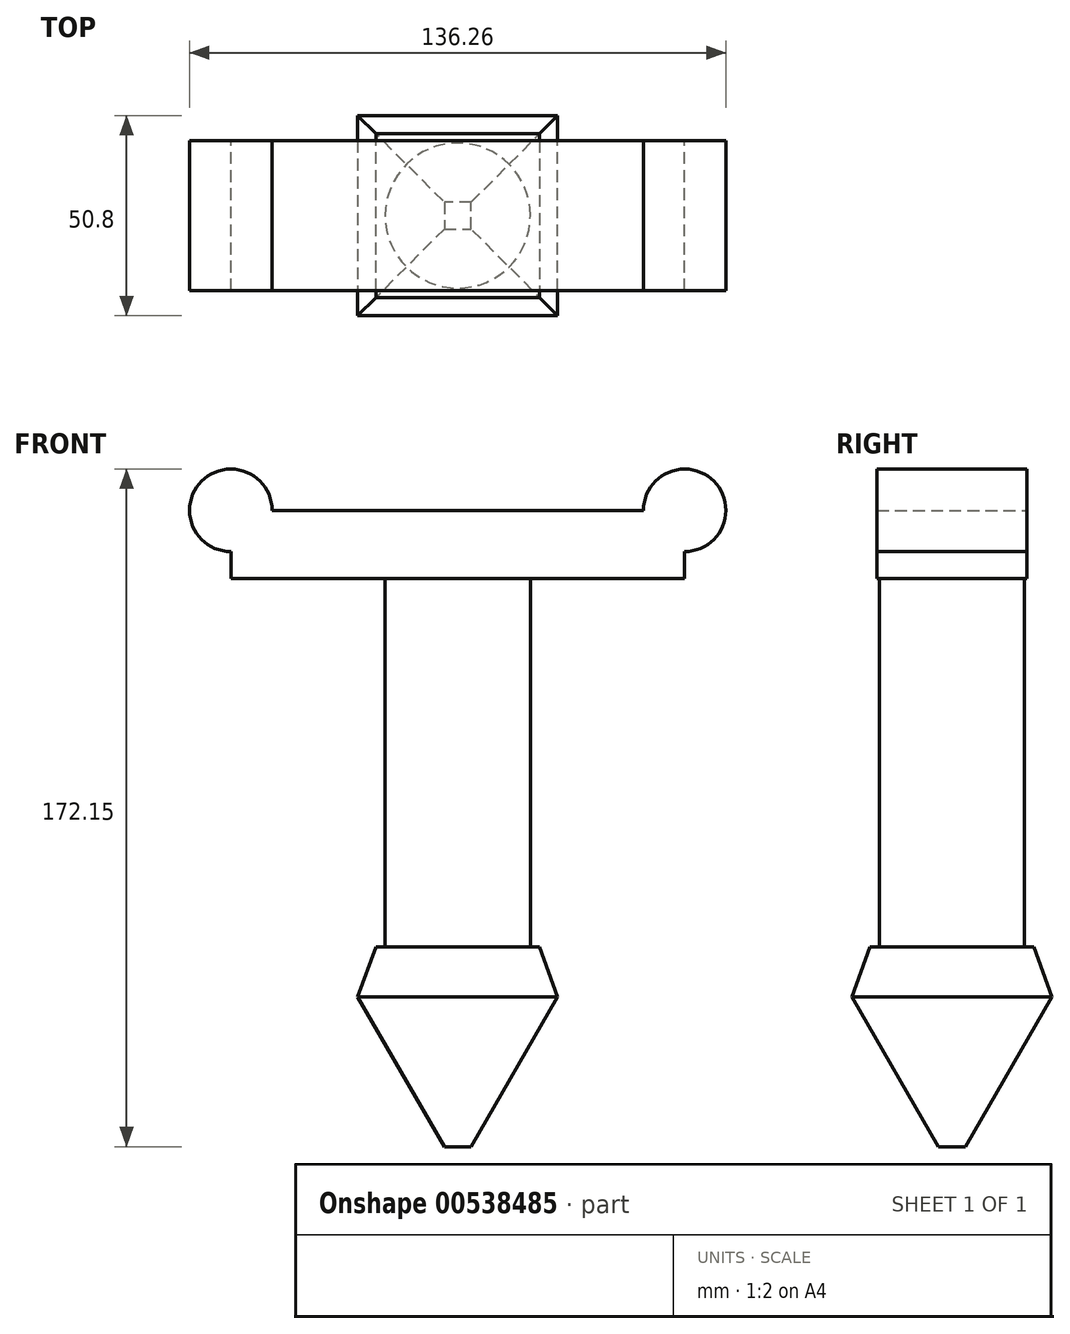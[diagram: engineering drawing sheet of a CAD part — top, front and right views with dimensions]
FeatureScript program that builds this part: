
annotation { "Feature Type Name" : "Feature", "Feature Type Description" : "" }
export const myFeature = defineFeature(function(context is Context, id is Id, definition is map)
    precondition{}
    {
        {
            var Q0;
            Q0=qCreatedBy(makeId("Top.planeOp"),FACE);
            var sketch = newSketch(context, id + "F0", { "sketchPlane" : qUnion([Q0])});
            skLineSegment(sketch, "E0.bottom", {"start": v(-25.4, 25.4) * mm, "end": v(25.4, 25.4) * mm});
            skLineSegment(sketch, "E0.top", {"start": v(-25.4, -25.4) * mm, "end": v(25.4, -25.4) * mm});
            skLineSegment(sketch, "E0.left", {"start": v(-25.4, 25.4) * mm, "end": v(-25.4, -25.4) * mm});
            skLineSegment(sketch, "E0.right", {"start": v(25.4, 25.4) * mm, "end": v(25.4, -25.4) * mm});
            skPoint(sketch, "E0.middle", {"position": v(0, 0) * mm});
            skSolve(sketch);
        }
        {
            var Q0;
            Q0 = qSketchRegion(id + "F0", true);
            extrude(context, id + "F1", {"entities" : qUnion([Q0]), "oppositeDirection" : true, "depth" : 38.1 * mm, "offsetDistance" : 25.4 * mm, "hasDraft" : true, "draftAngle" : 30 * degree, "draftPullDirection" : true});
        }
        {
            var Q0;
            Q0=makeQuery(id+"F1.opExtrude","CAP_FACE",FACE,{"disambiguationData":[OSD([sQuery(id+"F0.wireOp",EDGE,"E0.bottom"),sQuery(id+"F0.wireOp",EDGE,"E0.top"),sQuery(id+"F0.wireOp",EDGE,"E0.left"),sQuery(id+"F0.wireOp",EDGE,"E0.right")])],"isStart":true});
            extrude(context, id + "F2", {"entities" : qUnion([Q0]), "operationType" : NewBodyOperationType.ADD, "depth" : 12.7 * mm, "offsetDistance" : 25.4 * mm, "hasDraft" : true, "draftAngle" : 20 * degree, "draftPullDirection" : true});
        }
        {
            var Q0;
            Q0=makeQuery(id+"F2.opExtrude","CAP_FACE",FACE,{"disambiguationData":[OSD([sQuery(id+"F0.wireOp",EDGE,"E0.bottom"),sQuery(id+"F0.wireOp",EDGE,"E0.top"),sQuery(id+"F0.wireOp",EDGE,"E0.left"),sQuery(id+"F0.wireOp",EDGE,"E0.right")])],"isStart":false});
            var sketch = newSketch(context, id + "F3", { "sketchPlane" : qUnion([Q0])});
            skCircle(sketch, "E1", {"center": v(0, 0) * mm, "radius": 18.44 * mm});
            skSolve(sketch);
        }
        {
            var Q0;
            Q0 = qSketchRegion(id + "F3", true);
            extrude(context, id + "F4", {"entities" : qUnion([Q0]), "operationType" : NewBodyOperationType.ADD, "depth" : 101.6 * mm, "offsetDistance" : 25.4 * mm});
        }
        {
            var Q0;
            Q0=qCreatedBy(makeId("Front.planeOp"),FACE);
            var sketch = newSketch(context, id + "F5", { "sketchPlane" : qUnion([Q0])});
            skLineSegment(sketch, "E2.bottom", {"start": v(-47.16, 123.57) * mm, "end": v(47.16, 123.57) * mm});
            skLineSegment(sketch, "E2.top", {"start": v(-57.65, 106.28) * mm, "end": v(57.65, 106.28) * mm});
            skLineSegment(sketch, "E2.left", {"start": v(-57.65, 113.08) * mm, "end": v(-57.65, 106.28) * mm});
            skLineSegment(sketch, "E2.right", {"start": v(57.65, 113.08) * mm, "end": v(57.65, 106.28) * mm});
            skPoint(sketch, "E2.middle", {"position": v(0, 114.92) * mm});
            skArc(sketch, "E3", {"start": v(-47.16, 123.57) * mm, "mid": v(-65.06, 130.98) * mm, "end": v(-57.65, 113.08) * mm});
            skArc(sketch, "E4", {"start": v(57.65, 113.08) * mm, "mid": v(65.06, 130.98) * mm, "end": v(47.16, 123.57) * mm});
            skSolve(sketch);
        }
        {
            var Q0;
            Q0=makeQuery(id+"F5.imprint","IMPRINT",FACE,{"disambiguationData":[TD([[makeQuery(id+"F5.imprint","IMPRINT",EDGE,{"derivedFrom":sQuery(id+"F5.wireOp",EDGE,"E2.bottom")}),-1.0]])]});
            extrude(context, id + "F6", {"entities" : qUnion([Q0]), "operationType" : NewBodyOperationType.ADD, "depth" : 38.1 * mm, "offsetDistance" : 25.4 * mm, "symmetric" : true});
        }
        {
            var Q0;
            Q0 = qSketchRegion(id + "F5", true);
            extrude(context, id + "F7", {"entities" : qUnion([Q0]), "operationType" : NewBodyOperationType.ADD, "depth" : 38.1 * mm, "offsetDistance" : 25.4 * mm, "symmetric" : true});
        }
    });
